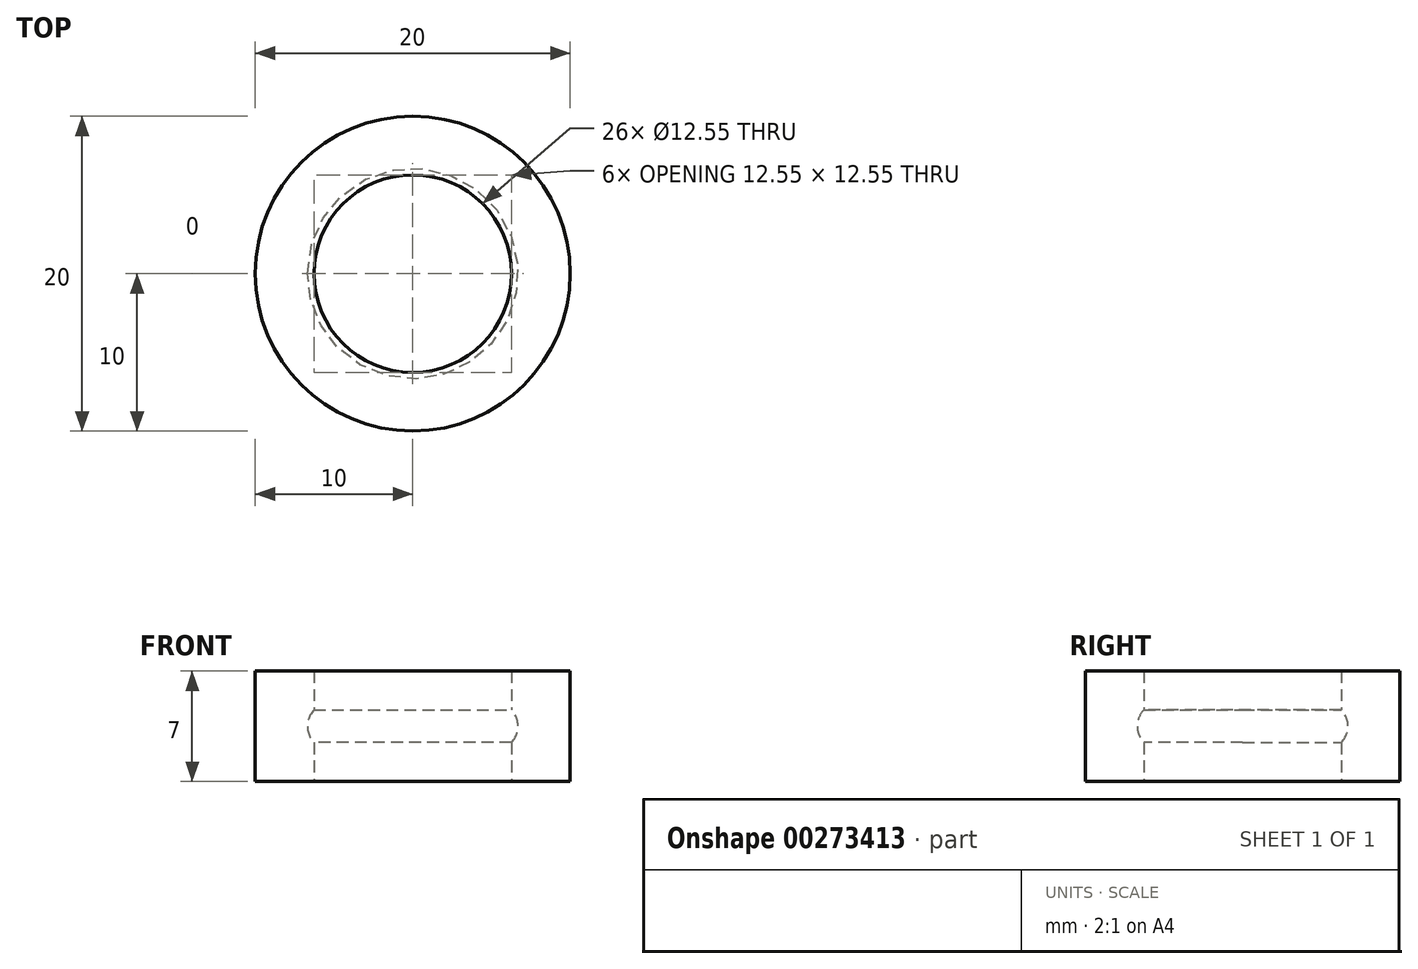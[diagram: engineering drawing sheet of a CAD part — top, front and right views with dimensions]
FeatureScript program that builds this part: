
annotation { "Feature Type Name" : "Feature", "Feature Type Description" : "" }
export const myFeature = defineFeature(function(context is Context, id is Id, definition is map)
    precondition{}
    {
        {
            var Q0;
            Q0=qCreatedBy(makeId("Top.planeOp"),FACE);
            var sketch = newSketch(context, id + "F0", { "sketchPlane" : qUnion([Q0])});
            skCircle(sketch, "E0", {"center": v(0, 0) * mm, "radius": 6.28 * mm});
            skCircle(sketch, "E1", {"center": v(0, 0) * mm, "radius": 10 * mm});
            skSolve(sketch);
        }
        {
            var Q0;
            Q0=makeQuery(id+"F0.imprint","IMPRINT",FACE,{"disambiguationData":[TD([[makeQuery(id+"F0.imprint","IMPRINT",EDGE,{"derivedFrom":sQuery(id+"F0.wireOp",EDGE,"E0")}),-1.0]])]});
            extrude(context, id + "F1", {"entities" : qUnion([Q0]), "depth" : 7 * mm});
        }
        {
            var Q0;
            Q0=qCreatedBy(makeId("Front.planeOp"),FACE);
            var sketch = newSketch(context, id + "F2", { "sketchPlane" : qUnion([Q0])});
            skLineSegment(sketch, "E2", {"start": v(0, 0) * mm, "end": v(0, 3.5) * mm, "construction": true});
            skLineSegment(sketch, "E3", {"start": v(0, 3.5) * mm, "end": v(-6.35, 3.5) * mm, "construction": true});
            skCircle(sketch, "E4", {"center": v(-5.2, 3.5) * mm, "radius": 1.49 * mm});
            skLineSegment(sketch, "E5", {"start": v(0, 6.02) * mm, "end": v(0, 0.84) * mm});
            skSolve(sketch);
        }
        {
            var Q0;
            Q0=makeQuery(id+"F2.imprint","IMPRINT",FACE,{"disambiguationData":[TD([[makeQuery(id+"F2.imprint","IMPRINT",EDGE,{"derivedFrom":sQuery(id+"F2.wireOp",EDGE,"E4")}),1.0]])]});
            var Q1;
            Q1=sQuery(id+"F2.wireOp",EDGE,"E5");
            revolve(context, id + "F3", {"operationType" : NewBodyOperationType.REMOVE, "entities" : qUnion([Q0]), "axis" : qUnion([Q1]), "revolveType" : RevolveType.FULL, "oppositeDirection" : true});
        }
    });
